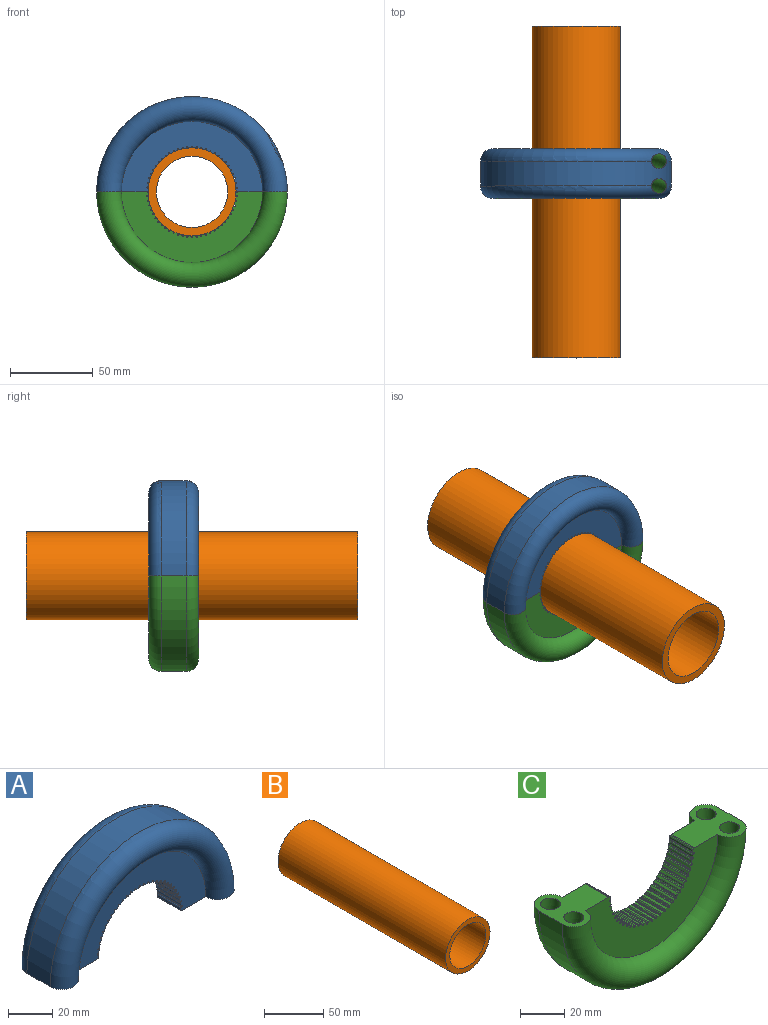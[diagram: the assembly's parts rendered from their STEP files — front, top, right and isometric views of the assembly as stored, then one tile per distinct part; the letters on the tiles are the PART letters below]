
ASSEMBLY  parts=3 mates=2
PART A: 191 faces, bbox 124.5x30x62.3 mm
  f0: cylinder r=57.5mm len=115mm, axis (0,1,0), area 2575.9mm2, adj f1,f3,f7,f8,f189,f190
  f1: torus R=50mm, axis (0,1,0), area 3629.1mm2, adj f0,f5,f7,f8,f190
  f2: torus R=50mm, axis (0,1,0), area 4103.8mm2, adj f7,f8,f190
  f3: torus R=50mm, axis (0,1,0), area 3629mm2, adj f0,f6,f7,f8,f189
  f4: torus R=50mm, axis (0,1,0), area 4103.8mm2, adj f7,f8,f189
  f5: plane 85x42.56mm, normal (0,1,0), area 1715.4mm2, adj f1,f7,f8,f9,f10,f11,f12,f13
  f6: plane 85x42.56mm, normal (0,-1,0), area 1715.4mm2, adj f3,f7,f8,f9,f10,f11,f12,f13
  f7: plane 30x30mm, normal (0,0,-1), area 499.5mm2, adj f0,f1,f2,f3,f4,f5,f6,f10
  f8: plane 30x30mm, normal (0,0,-1), area 499.5mm2, adj f0,f1,f2,f3,f4,f5,f6,f9
  f9: cylinder r=27.5mm len=15mm, axis (0,1,0), area 0.9mm2, adj f5,f6,f8,f188
  f10: plane 15x0.6mm, normal (0.21,0,-0.98), area 9.2mm2, adj f5,f6,f7,f11
  f11: cylinder r=0.5mm len=15mm, axis (0,1,0), area 9.8mm2, adj f5,f6,f10,f12
  f12: plane 15x1.18mm, normal (1,0,-0.04), area 17.7mm2, adj f5,f6,f11,f13
  f13: cylinder r=0.5mm len=15mm, axis (0,1,0), area 9.8mm2, adj f5,f6,f12,f14
  f14: plane 15x0.23mm, normal (0.3,0,0.95), area 3.6mm2, adj f5,f6,f13,f15
  f15: cylinder r=0.3mm len=15mm, axis (0,1,0), area 12.3mm2, adj f5,f6,f14,f16
  f16: plane 15x0.24mm, normal (0.11,0,-0.99), area 3.6mm2, adj f5,f6,f15,f17
  f17: cylinder r=0.5mm len=15mm, axis (0,1,0), area 9.8mm2, adj f5,f6,f16,f18
  f18: plane 15x1.17mm, normal (0.99,0,-0.15), area 17.7mm2, adj f5,f6,f17,f19
  f19: cylinder r=0.5mm len=15mm, axis (0,1,0), area 9.8mm2, adj f5,f6,f18,f20
  f20: plane 15x0.22mm, normal (0.4,0,0.92), area 3.6mm2, adj f5,f6,f19,f21
  f21: cylinder r=0.3mm len=15mm, axis (0,1,0), area 12.3mm2, adj f5,f6,f20,f22
  f22: plane 15x0.24mm, normal (0,0,-1), area 3.6mm2, adj f5,f6,f21,f23
  f23: cylinder r=0.5mm len=15mm, axis (0,1,0), area 9.8mm2, adj f5,f6,f22,f24
  f24: plane 15x1.14mm, normal (0.97,0,-0.25), area 17.7mm2, adj f5,f6,f23,f25
  f25: cylinder r=0.5mm len=15mm, axis (0,1,0), area 9.8mm2, adj f5,f6,f24,f26
  f26: plane 15x0.21mm, normal (0.49,0,0.87), area 3.6mm2, adj f5,f6,f25,f27
  f27: cylinder r=0.3mm len=15mm, axis (0,1,0), area 12.3mm2, adj f5,f6,f26,f28
  f28: plane 15x0.24mm, normal (-0.1,0,-0.99), area 3.6mm2, adj f5,f6,f27,f29
  f29: cylinder r=0.5mm len=15mm, axis (0,1,0), area 9.8mm2, adj f5,f6,f28,f30
  f30: plane 15x1.1mm, normal (0.94,0,-0.35), area 17.7mm2, adj f5,f6,f29,f31
  f31: cylinder r=0.5mm len=15mm, axis (0,1,0), area 9.8mm2, adj f5,f6,f30,f32
  f32: plane 15x0.2mm, normal (0.58,0,0.81), area 3.6mm2, adj f5,f6,f31,f33
  f33: cylinder r=0.3mm len=15mm, axis (0,1,0), area 12.3mm2, adj f5,f6,f32,f34
  f34: plane 15x0.23mm, normal (-0.21,0,-0.98), area 3.6mm2, adj f5,f6,f33,f35
  f35: cylinder r=0.5mm len=15mm, axis (0,1,0), area 9.8mm2, adj f5,f6,f34,f36
  f36: plane 15x1.05mm, normal (0.89,0,-0.45), area 17.7mm2, adj f5,f6,f35,f37
  f37: cylinder r=0.5mm len=15mm, axis (0,1,0), area 9.8mm2, adj f5,f6,f36,f38
  f38: plane 15x0.18mm, normal (0.66,0,0.75), area 3.6mm2, adj f5,f6,f37,f39
  f39: cylinder r=0.3mm len=15mm, axis (0,1,0), area 12.3mm2, adj f5,f6,f38,f40
  f40: plane 15x0.23mm, normal (-0.31,0,-0.95), area 3.6mm2, adj f5,f6,f39,f41
  f41: cylinder r=0.5mm len=15mm, axis (0,1,0), area 9.8mm2, adj f5,f6,f40,f42
  f42: plane 15x0.99mm, normal (0.84,0,-0.54), area 17.7mm2, adj f5,f6,f41,f43
  f43: cylinder r=0.5mm len=15mm, axis (0,1,0), area 9.8mm2, adj f5,f6,f42,f44
  f44: plane 15x0.18mm, normal (0.74,0,0.68), area 3.6mm2, adj f5,f6,f43,f45
  f45: cylinder r=0.3mm len=15mm, axis (0,1,0), area 12.3mm2, adj f5,f6,f44,f46
  f46: plane 15x0.22mm, normal (-0.41,0,-0.91), area 3.6mm2, adj f5,f6,f45,f47
  f47: cylinder r=0.5mm len=15mm, axis (0,1,0), area 9.8mm2, adj f5,f6,f46,f48
  f48: plane 15x0.92mm, normal (0.78,0,-0.63), area 17.7mm2, adj f5,f6,f47,f49
  f49: cylinder r=0.5mm len=15mm, axis (0,1,0), area 9.8mm2, adj f5,f6,f48,f50
  f50: plane 15x0.19mm, normal (0.8,0,0.59), area 3.6mm2, adj f5,f6,f49,f51
  f51: cylinder r=0.3mm len=15mm, axis (0,1,0), area 12.3mm2, adj f5,f6,f50,f52
  f52: plane 15x0.21mm, normal (-0.5,0,-0.87), area 3.6mm2, adj f5,f6,f51,f53
  f53: cylinder r=0.5mm len=15mm, axis (0,1,0), area 9.8mm2, adj f5,f6,f52,f54
  f54: plane 15x0.84mm, normal (0.71,0,-0.7), area 17.7mm2, adj f5,f6,f53,f55
  f55: cylinder r=0.5mm len=15mm, axis (0,1,0), area 9.8mm2, adj f5,f6,f54,f56
  f56: plane 15x0.21mm, normal (0.86,0,0.51), area 3.6mm2, adj f5,f6,f55,f57
  f57: cylinder r=0.3mm len=15mm, axis (0,1,0), area 12.3mm2, adj f5,f6,f56,f58
  f58: plane 15x0.19mm, normal (-0.59,0,-0.81), area 3.6mm2, adj f5,f6,f57,f59
  f59: cylinder r=0.5mm len=15mm, axis (0,1,0), area 9.8mm2, adj f5,f6,f58,f60
  f60: plane 15x0.92mm, normal (0.63,0,-0.78), area 17.7mm2, adj f5,f6,f59,f61
  f61: cylinder r=0.5mm len=15mm, axis (0,1,0), area 9.8mm2, adj f5,f6,f60,f62
  f62: plane 15x0.22mm, normal (0.91,0,0.41), area 3.6mm2, adj f5,f6,f61,f63
  f63: cylinder r=0.3mm len=15mm, axis (0,1,0), area 12.3mm2, adj f5,f6,f62,f64
  f64: plane 15x0.18mm, normal (-0.67,0,-0.74), area 3.6mm2, adj f5,f6,f63,f65
  f65: cylinder r=0.5mm len=15mm, axis (0,1,0), area 9.8mm2, adj f5,f6,f64,f66
  f66: plane 15x0.99mm, normal (0.55,0,-0.84), area 17.7mm2, adj f5,f6,f65,f67
  f67: cylinder r=0.5mm len=15mm, axis (0,1,0), area 9.8mm2, adj f5,f6,f66,f68
  f68: plane 15x0.23mm, normal (0.95,0,0.31), area 3.6mm2, adj f5,f6,f67,f69
  f69: cylinder r=0.3mm len=15mm, axis (0,1,0), area 12.3mm2, adj f5,f6,f68,f70
  f70: plane 15x0.18mm, normal (-0.74,0,-0.67), area 3.6mm2, adj f5,f6,f69,f71
  f71: cylinder r=0.5mm len=15mm, axis (0,1,0), area 9.8mm2, adj f5,f6,f70,f72
  f72: plane 15x1.05mm, normal (0.46,0,-0.89), area 17.7mm2, adj f5,f6,f71,f73
  f73: cylinder r=0.5mm len=15mm, axis (0,1,0), area 9.8mm2, adj f5,f6,f72,f74
  f74: plane 15x0.23mm, normal (0.98,0,0.21), area 3.6mm2, adj f5,f6,f73,f75
  f75: cylinder r=0.3mm len=15mm, axis (0,1,0), area 12.3mm2, adj f5,f6,f74,f76
  f76: plane 15x0.19mm, normal (-0.81,0,-0.59), area 3.6mm2, adj f5,f6,f75,f77
  f77: cylinder r=0.5mm len=15mm, axis (0,1,0), area 9.8mm2, adj f5,f6,f76,f78
  f78: plane 15x1.1mm, normal (0.36,0,-0.93), area 17.7mm2, adj f5,f6,f77,f79
  f79: cylinder r=0.5mm len=15mm, axis (0,1,0), area 9.8mm2, adj f5,f6,f78,f80
  f80: plane 15x0.24mm, normal (0.99,0,0.11), area 3.6mm2, adj f5,f6,f79,f81
  f81: cylinder r=0.3mm len=15mm, axis (0,1,0), area 12.3mm2, adj f5,f6,f80,f82
  f82: plane 15x0.21mm, normal (-0.87,0,-0.5), area 3.6mm2, adj f5,f6,f81,f83
  f83: cylinder r=0.5mm len=15mm, axis (0,1,0), area 9.8mm2, adj f5,f6,f82,f84
  f84: plane 15x1.14mm, normal (0.26,0,-0.97), area 17.7mm2, adj f5,f6,f83,f85
  f85: cylinder r=0.5mm len=15mm, axis (0,1,0), area 9.8mm2, adj f5,f6,f84,f86
  f86: plane 15x0.24mm, normal (1,0,0), area 3.6mm2, adj f5,f6,f85,f87
  f87: cylinder r=0.3mm len=15mm, axis (0,1,0), area 12.3mm2, adj f5,f6,f86,f88
  f88: plane 15x0.22mm, normal (-0.92,0,-0.4), area 3.6mm2, adj f5,f6,f87,f89
  f89: cylinder r=0.5mm len=15mm, axis (0,1,0), area 9.8mm2, adj f5,f6,f88,f90
  f90: plane 15x1.17mm, normal (0.16,0,-0.99), area 17.7mm2, adj f5,f6,f89,f91
  f91: cylinder r=0.5mm len=15mm, axis (0,1,0), area 9.8mm2, adj f5,f6,f90,f92
  f92: plane 15x0.24mm, normal (0.99,0,-0.1), area 3.6mm2, adj f5,f6,f91,f93
  f93: cylinder r=0.3mm len=15mm, axis (0,1,0), area 12.3mm2, adj f5,f6,f92,f94
  f94: plane 15x0.23mm, normal (-0.95,0,-0.3), area 3.6mm2, adj f5,f6,f93,f95
  f95: cylinder r=0.5mm len=15mm, axis (0,1,0), area 9.8mm2, adj f5,f6,f94,f96
  f96: plane 15x1.18mm, normal (0.05,0,-1), area 17.7mm2, adj f5,f6,f95,f97
  f97: cylinder r=0.5mm len=15mm, axis (0,1,0), area 9.8mm2, adj f5,f6,f96,f98
  f98: plane 15x0.23mm, normal (0.98,0,-0.21), area 3.6mm2, adj f5,f6,f97,f99
  f99: cylinder r=0.3mm len=15mm, axis (0,1,0), area 12.3mm2, adj f5,f6,f98,f100
  f100: plane 15x0.23mm, normal (-0.98,0,-0.2), area 3.6mm2, adj f5,f6,f99,f101
  f101: cylinder r=0.5mm len=15mm, axis (0,1,0), area 9.8mm2, adj f5,f6,f100,f102
  f102: plane 15x1.18mm, normal (-0.05,0,-1), area 17.7mm2, adj f5,f6,f101,f103
  f103: cylinder r=0.5mm len=15mm, axis (0,1,0), area 9.8mm2, adj f5,f6,f102,f104
  f104: plane 15x0.23mm, normal (0.95,0,-0.31), area 3.6mm2, adj f5,f6,f103,f105
  f105: cylinder r=0.3mm len=15mm, axis (0,1,0), area 12.3mm2, adj f5,f6,f104,f106
  f106: plane 15x0.24mm, normal (-1,0,-0.1), area 3.6mm2, adj f5,f6,f105,f107
  f107: cylinder r=0.5mm len=15mm, axis (0,1,0), area 9.8mm2, adj f5,f6,f106,f108
  f108: plane 15x1.17mm, normal (-0.16,0,-0.99), area 17.7mm2, adj f5,f6,f107,f109
  f109: cylinder r=0.5mm len=15mm, axis (0,1,0), area 9.8mm2, adj f5,f6,f108,f110
  f110: plane 15x0.22mm, normal (0.91,0,-0.41), area 3.6mm2, adj f5,f6,f109,f111
  f111: cylinder r=0.3mm len=15mm, axis (0,1,0), area 12.3mm2, adj f5,f6,f110,f112
  f112: plane 15x0.24mm, normal (-1,0,0.01), area 3.6mm2, adj f5,f6,f111,f113
  f113: cylinder r=0.5mm len=15mm, axis (0,1,0), area 9.8mm2, adj f5,f6,f112,f114
  f114: plane 15x1.14mm, normal (-0.26,0,-0.97), area 17.7mm2, adj f5,f6,f113,f115
  f115: cylinder r=0.5mm len=15mm, axis (0,1,0), area 9.8mm2, adj f5,f6,f114,f116
  f116: plane 15x0.21mm, normal (0.87,0,-0.5), area 3.6mm2, adj f5,f6,f115,f117
  f117: cylinder r=0.3mm len=15mm, axis (0,1,0), area 12.3mm2, adj f5,f6,f116,f118
  f118: plane 15x0.24mm, normal (-0.99,0,0.11), area 3.6mm2, adj f5,f6,f117,f119
  f119: cylinder r=0.5mm len=15mm, axis (0,1,0), area 9.8mm2, adj f5,f6,f118,f120
  f120: plane 15x1.1mm, normal (-0.36,0,-0.93), area 17.7mm2, adj f5,f6,f119,f121
  f121: cylinder r=0.5mm len=15mm, axis (0,1,0), area 9.8mm2, adj f5,f6,f120,f122
  f122: plane 15x0.19mm, normal (0.81,0,-0.59), area 3.6mm2, adj f5,f6,f121,f123
  f123: cylinder r=0.3mm len=15mm, axis (0,1,0), area 12.3mm2, adj f5,f6,f122,f124
  f124: plane 15x0.23mm, normal (-0.98,0,0.21), area 3.6mm2, adj f5,f6,f123,f125
  f125: cylinder r=0.5mm len=15mm, axis (0,1,0), area 9.8mm2, adj f5,f6,f124,f126
  f126: plane 15x1.05mm, normal (-0.46,0,-0.89), area 17.7mm2, adj f5,f6,f125,f127
  f127: cylinder r=0.5mm len=15mm, axis (0,1,0), area 9.8mm2, adj f5,f6,f126,f128
  f128: plane 15x0.18mm, normal (0.74,0,-0.67), area 3.6mm2, adj f5,f6,f127,f129
  f129: cylinder r=0.3mm len=15mm, axis (0,1,0), area 12.3mm2, adj f5,f6,f128,f130
  f130: plane 15x0.23mm, normal (-0.95,0,0.32), area 3.6mm2, adj f5,f6,f129,f131
  f131: cylinder r=0.5mm len=15mm, axis (0,1,0), area 9.8mm2, adj f5,f6,f130,f132
  f132: plane 15x0.99mm, normal (-0.55,0,-0.84), area 17.7mm2, adj f5,f6,f131,f133
  f133: cylinder r=0.5mm len=15mm, axis (0,1,0), area 9.8mm2, adj f5,f6,f132,f134
  f134: plane 15x0.18mm, normal (0.67,0,-0.74), area 3.6mm2, adj f5,f6,f133,f135
  f135: cylinder r=0.3mm len=15mm, axis (0,1,0), area 12.3mm2, adj f5,f6,f134,f136
  f136: plane 15x0.22mm, normal (-0.91,0,0.41), area 3.6mm2, adj f5,f6,f135,f137
  f137: cylinder r=0.5mm len=15mm, axis (0,1,0), area 9.8mm2, adj f5,f6,f136,f138
  f138: plane 15x0.91mm, normal (-0.63,0,-0.77), area 17.7mm2, adj f5,f6,f137,f139
  f139: cylinder r=0.5mm len=15mm, axis (0,1,0), area 9.8mm2, adj f5,f6,f138,f140
  f140: plane 15x0.19mm, normal (0.59,0,-0.81), area 3.6mm2, adj f5,f6,f139,f141
  f141: cylinder r=0.3mm len=15mm, axis (0,1,0), area 12.3mm2, adj f5,f6,f140,f142
  f142: plane 15x0.21mm, normal (-0.86,0,0.51), area 3.6mm2, adj f5,f6,f141,f143
  f143: cylinder r=0.5mm len=15mm, axis (0,1,0), area 9.8mm2, adj f5,f6,f142,f144
  f144: plane 15x0.84mm, normal (-0.71,0,-0.7), area 17.7mm2, adj f5,f6,f143,f145
  f145: cylinder r=0.5mm len=15mm, axis (0,1,0), area 9.8mm2, adj f5,f6,f144,f146
  f146: plane 15x0.21mm, normal (0.5,0,-0.87), area 3.6mm2, adj f5,f6,f145,f147
  f147: cylinder r=0.3mm len=15mm, axis (0,1,0), area 12.3mm2, adj f5,f6,f146,f148
  f148: plane 15x0.19mm, normal (-0.8,0,0.6), area 3.6mm2, adj f5,f6,f147,f149
  f149: cylinder r=0.5mm len=15mm, axis (0,1,0), area 9.8mm2, adj f5,f6,f148,f150
  f150: plane 15x0.92mm, normal (-0.78,0,-0.62), area 17.7mm2, adj f5,f6,f149,f151
  f151: cylinder r=0.5mm len=15mm, axis (0,1,0), area 9.8mm2, adj f5,f6,f150,f152
  f152: plane 15x0.22mm, normal (0.4,0,-0.91), area 3.6mm2, adj f5,f6,f151,f153
  f153: cylinder r=0.3mm len=15mm, axis (0,1,0), area 12.3mm2, adj f5,f6,f152,f154
  f154: plane 15x0.18mm, normal (-0.74,0,0.68), area 3.6mm2, adj f5,f6,f153,f155
  f155: cylinder r=0.5mm len=15mm, axis (0,1,0), area 9.8mm2, adj f5,f6,f154,f156
  f156: plane 15x0.99mm, normal (-0.84,0,-0.54), area 17.7mm2, adj f5,f6,f155,f157
  f157: cylinder r=0.5mm len=15mm, axis (0,1,0), area 9.8mm2, adj f5,f6,f156,f158
  f158: plane 15x0.23mm, normal (0.31,0,-0.95), area 3.6mm2, adj f5,f6,f157,f159
  f159: cylinder r=0.3mm len=15mm, axis (0,1,0), area 12.3mm2, adj f5,f6,f158,f160
  f160: plane 15x0.18mm, normal (-0.66,0,0.75), area 3.6mm2, adj f5,f6,f159,f161
  f161: cylinder r=0.5mm len=15mm, axis (0,1,0), area 9.8mm2, adj f5,f6,f160,f162
  f162: plane 15x1.06mm, normal (-0.89,0,-0.45), area 17.7mm2, adj f5,f6,f161,f163
  f163: cylinder r=0.5mm len=15mm, axis (0,1,0), area 9.8mm2, adj f5,f6,f162,f164
  f164: plane 15x0.23mm, normal (0.2,0,-0.98), area 3.6mm2, adj f5,f6,f163,f165
  f165: cylinder r=0.3mm len=15mm, axis (0,1,0), area 12.3mm2, adj f5,f6,f164,f166
  f166: plane 15x0.2mm, normal (-0.58,0,0.82), area 3.6mm2, adj f5,f6,f165,f167
  f167: cylinder r=0.5mm len=15mm, axis (0,1,0), area 9.8mm2, adj f5,f6,f166,f168
  f168: plane 15x1.11mm, normal (-0.94,0,-0.35), area 17.7mm2, adj f5,f6,f167,f169
  f169: cylinder r=0.5mm len=15mm, axis (0,1,0), area 9.8mm2, adj f5,f6,f168,f170
  f170: plane 15x0.24mm, normal (0.1,0,-0.99), area 3.6mm2, adj f5,f6,f169,f171
  f171: cylinder r=0.3mm len=15mm, axis (0,1,0), area 12.3mm2, adj f5,f6,f170,f172
  f172: plane 15x0.21mm, normal (-0.49,0,0.87), area 3.6mm2, adj f5,f6,f171,f173
  f173: cylinder r=0.5mm len=15mm, axis (0,1,0), area 9.8mm2, adj f5,f6,f172,f174
  f174: plane 15x1.14mm, normal (-0.97,0,-0.25), area 17.7mm2, adj f5,f6,f173,f175
  f175: cylinder r=0.5mm len=15mm, axis (0,1,0), area 9.8mm2, adj f5,f6,f174,f176
  f176: plane 15x0.24mm, normal (-0.01,0,-1), area 3.6mm2, adj f5,f6,f175,f177
  f177: cylinder r=0.3mm len=15mm, axis (0,1,0), area 12.3mm2, adj f5,f6,f176,f178
  f178: plane 15x0.22mm, normal (-0.4,0,0.92), area 3.6mm2, adj f5,f6,f177,f179
  f179: cylinder r=0.5mm len=15mm, axis (0,1,0), area 9.8mm2, adj f5,f6,f178,f180
  f180: plane 15x1.17mm, normal (-0.99,0,-0.15), area 17.7mm2, adj f5,f6,f179,f181
  f181: cylinder r=0.5mm len=15mm, axis (0,1,0), area 9.8mm2, adj f5,f6,f180,f182
  f182: plane 15x0.24mm, normal (-0.11,0,-0.99), area 3.6mm2, adj f5,f6,f181,f183
  f183: cylinder r=0.3mm len=15mm, axis (0,1,0), area 12.3mm2, adj f5,f6,f182,f184
  f184: plane 15x0.23mm, normal (-0.3,0,0.96), area 3.6mm2, adj f5,f6,f183,f185
  f185: cylinder r=0.5mm len=15mm, axis (0,1,0), area 9.8mm2, adj f5,f6,f184,f186
  f186: plane 15x1.18mm, normal (-1,0,-0.04), area 17.7mm2, adj f5,f6,f185,f187
  f187: cylinder r=0.5mm len=15mm, axis (0,1,0), area 9.8mm2, adj f5,f6,f186,f188
  f188: plane 15x0.6mm, normal (-0.21,0,-0.98), area 9.2mm2, adj f5,f6,f9,f187
  f189: cylinder r=4.5mm len=35.16mm, axis (0,0,-1), area 434.3mm2, adj f0,f3,f4,f8
  f190: cylinder r=4.5mm len=35.16mm, axis (0,0,-1), area 434.3mm2, adj f0,f1,f2,f8
PART B: 4 faces, bbox 53x200x53 mm
  f0: cylinder r=21.5mm len=200mm, axis (0,1,0), area 27017.7mm2, adj f2,f3
  f1: cylinder r=26.5mm len=200mm, axis (0,1,0), area 33300.9mm2, adj f2,f3
  f2: plane 53x53mm, normal (0,-1,0), area 754mm2, adj f0,f1
  f3: plane 53x53mm, normal (0,1,0), area 754mm2, adj f0,f1
PART C: 189 faces, bbox 124.5x30x62.3 mm
  f0: cylinder r=57.5mm len=115mm, axis (0,1,0), area 2709.6mm2, adj f1,f5,f7,f8
  f1: torus R=50mm, axis (0,1,0), area 3701.1mm2, adj f0,f2,f7,f8
  f2: plane 85x42.56mm, normal (0,1,0), area 1715.4mm2, adj f1,f7,f8,f9,f10,f11,f12,f13
  f3: plane 85x42.56mm, normal (0,-1,0), area 1715.4mm2, adj f5,f7,f8,f9,f10,f11,f12,f13
  f4: torus R=50mm, axis (0,1,0), area 4441.3mm2, adj f7,f8
  f5: torus R=50mm, axis (0,1,0), area 3701.1mm2, adj f0,f3,f7,f8
  f6: torus R=50mm, axis (0,1,0), area 4441.3mm2, adj f7,f8
  f7: plane 30x30mm, normal (0,0,1), area 499.5mm2, adj f0,f1,f2,f3,f4,f5,f6,f10
  f8: plane 30x30mm, normal (0,0,1), area 499.5mm2, adj f0,f1,f2,f3,f4,f5,f6,f9
  f9: cylinder r=27.5mm len=15mm, axis (0,1,0), area 0.9mm2, adj f2,f3,f8,f188
  f10: plane 15x0.6mm, normal (-0.21,0,0.98), area 9.2mm2, adj f2,f3,f7,f11
  f11: cylinder r=0.5mm len=15mm, axis (0,1,0), area 9.8mm2, adj f2,f3,f10,f12
  f12: plane 15x1.18mm, normal (-1,0,0.04), area 17.7mm2, adj f2,f3,f11,f13
  f13: cylinder r=0.5mm len=15mm, axis (0,1,0), area 9.8mm2, adj f2,f3,f12,f14
  f14: plane 15x0.23mm, normal (-0.3,0,-0.95), area 3.6mm2, adj f2,f3,f13,f15
  f15: cylinder r=0.3mm len=15mm, axis (0,1,0), area 12.3mm2, adj f2,f3,f14,f16
  f16: plane 15x0.24mm, normal (-0.11,0,0.99), area 3.6mm2, adj f2,f3,f15,f17
  f17: cylinder r=0.5mm len=15mm, axis (0,1,0), area 9.8mm2, adj f2,f3,f16,f18
  f18: plane 15x1.17mm, normal (-0.99,0,0.15), area 17.7mm2, adj f2,f3,f17,f19
  f19: cylinder r=0.5mm len=15mm, axis (0,1,0), area 9.8mm2, adj f2,f3,f18,f20
  f20: plane 15x0.22mm, normal (-0.4,0,-0.92), area 3.6mm2, adj f2,f3,f19,f21
  f21: cylinder r=0.3mm len=15mm, axis (0,1,0), area 12.3mm2, adj f2,f3,f20,f22
  f22: plane 15x0.24mm, normal (0,0,1), area 3.6mm2, adj f2,f3,f21,f23
  f23: cylinder r=0.5mm len=15mm, axis (0,1,0), area 9.8mm2, adj f2,f3,f22,f24
  f24: plane 15x1.14mm, normal (-0.97,0,0.25), area 17.7mm2, adj f2,f3,f23,f25
  f25: cylinder r=0.5mm len=15mm, axis (0,1,0), area 9.8mm2, adj f2,f3,f24,f26
  f26: plane 15x0.21mm, normal (-0.49,0,-0.87), area 3.6mm2, adj f2,f3,f25,f27
  f27: cylinder r=0.3mm len=15mm, axis (0,1,0), area 12.3mm2, adj f2,f3,f26,f28
  f28: plane 15x0.24mm, normal (0.1,0,0.99), area 3.6mm2, adj f2,f3,f27,f29
  f29: cylinder r=0.5mm len=15mm, axis (0,1,0), area 9.8mm2, adj f2,f3,f28,f30
  f30: plane 15x1.1mm, normal (-0.94,0,0.35), area 17.7mm2, adj f2,f3,f29,f31
  f31: cylinder r=0.5mm len=15mm, axis (0,1,0), area 9.8mm2, adj f2,f3,f30,f32
  f32: plane 15x0.2mm, normal (-0.58,0,-0.81), area 3.6mm2, adj f2,f3,f31,f33
  f33: cylinder r=0.3mm len=15mm, axis (0,1,0), area 12.3mm2, adj f2,f3,f32,f34
  f34: plane 15x0.23mm, normal (0.21,0,0.98), area 3.6mm2, adj f2,f3,f33,f35
  f35: cylinder r=0.5mm len=15mm, axis (0,1,0), area 9.8mm2, adj f2,f3,f34,f36
  f36: plane 15x1.05mm, normal (-0.89,0,0.45), area 17.7mm2, adj f2,f3,f35,f37
  f37: cylinder r=0.5mm len=15mm, axis (0,1,0), area 9.8mm2, adj f2,f3,f36,f38
  f38: plane 15x0.18mm, normal (-0.66,0,-0.75), area 3.6mm2, adj f2,f3,f37,f39
  f39: cylinder r=0.3mm len=15mm, axis (0,1,0), area 12.3mm2, adj f2,f3,f38,f40
  f40: plane 15x0.23mm, normal (0.31,0,0.95), area 3.6mm2, adj f2,f3,f39,f41
  f41: cylinder r=0.5mm len=15mm, axis (0,1,0), area 9.8mm2, adj f2,f3,f40,f42
  f42: plane 15x0.99mm, normal (-0.84,0,0.54), area 17.7mm2, adj f2,f3,f41,f43
  f43: cylinder r=0.5mm len=15mm, axis (0,1,0), area 9.8mm2, adj f2,f3,f42,f44
  f44: plane 15x0.18mm, normal (-0.74,0,-0.68), area 3.6mm2, adj f2,f3,f43,f45
  f45: cylinder r=0.3mm len=15mm, axis (0,1,0), area 12.3mm2, adj f2,f3,f44,f46
  f46: plane 15x0.22mm, normal (0.41,0,0.91), area 3.6mm2, adj f2,f3,f45,f47
  f47: cylinder r=0.5mm len=15mm, axis (0,1,0), area 9.8mm2, adj f2,f3,f46,f48
  f48: plane 15x0.92mm, normal (-0.78,0,0.63), area 17.7mm2, adj f2,f3,f47,f49
  f49: cylinder r=0.5mm len=15mm, axis (0,1,0), area 9.8mm2, adj f2,f3,f48,f50
  f50: plane 15x0.19mm, normal (-0.8,0,-0.59), area 3.6mm2, adj f2,f3,f49,f51
  f51: cylinder r=0.3mm len=15mm, axis (0,1,0), area 12.3mm2, adj f2,f3,f50,f52
  f52: plane 15x0.21mm, normal (0.5,0,0.87), area 3.6mm2, adj f2,f3,f51,f53
  f53: cylinder r=0.5mm len=15mm, axis (0,1,0), area 9.8mm2, adj f2,f3,f52,f54
  f54: plane 15x0.84mm, normal (-0.71,0,0.7), area 17.7mm2, adj f2,f3,f53,f55
  f55: cylinder r=0.5mm len=15mm, axis (0,1,0), area 9.8mm2, adj f2,f3,f54,f56
  f56: plane 15x0.21mm, normal (-0.86,0,-0.51), area 3.6mm2, adj f2,f3,f55,f57
  f57: cylinder r=0.3mm len=15mm, axis (0,1,0), area 12.3mm2, adj f2,f3,f56,f58
  f58: plane 15x0.19mm, normal (0.59,0,0.81), area 3.6mm2, adj f2,f3,f57,f59
  f59: cylinder r=0.5mm len=15mm, axis (0,1,0), area 9.8mm2, adj f2,f3,f58,f60
  f60: plane 15x0.92mm, normal (-0.63,0,0.78), area 17.7mm2, adj f2,f3,f59,f61
  f61: cylinder r=0.5mm len=15mm, axis (0,1,0), area 9.8mm2, adj f2,f3,f60,f62
  f62: plane 15x0.22mm, normal (-0.91,0,-0.41), area 3.6mm2, adj f2,f3,f61,f63
  f63: cylinder r=0.3mm len=15mm, axis (0,1,0), area 12.3mm2, adj f2,f3,f62,f64
  f64: plane 15x0.18mm, normal (0.67,0,0.74), area 3.6mm2, adj f2,f3,f63,f65
  f65: cylinder r=0.5mm len=15mm, axis (0,1,0), area 9.8mm2, adj f2,f3,f64,f66
  f66: plane 15x0.99mm, normal (-0.55,0,0.84), area 17.7mm2, adj f2,f3,f65,f67
  f67: cylinder r=0.5mm len=15mm, axis (0,1,0), area 9.8mm2, adj f2,f3,f66,f68
  f68: plane 15x0.23mm, normal (-0.95,0,-0.31), area 3.6mm2, adj f2,f3,f67,f69
  f69: cylinder r=0.3mm len=15mm, axis (0,1,0), area 12.3mm2, adj f2,f3,f68,f70
  f70: plane 15x0.18mm, normal (0.74,0,0.67), area 3.6mm2, adj f2,f3,f69,f71
  f71: cylinder r=0.5mm len=15mm, axis (0,1,0), area 9.8mm2, adj f2,f3,f70,f72
  f72: plane 15x1.05mm, normal (-0.46,0,0.89), area 17.7mm2, adj f2,f3,f71,f73
  f73: cylinder r=0.5mm len=15mm, axis (0,1,0), area 9.8mm2, adj f2,f3,f72,f74
  f74: plane 15x0.23mm, normal (-0.98,0,-0.21), area 3.6mm2, adj f2,f3,f73,f75
  f75: cylinder r=0.3mm len=15mm, axis (0,1,0), area 12.3mm2, adj f2,f3,f74,f76
  f76: plane 15x0.19mm, normal (0.81,0,0.59), area 3.6mm2, adj f2,f3,f75,f77
  f77: cylinder r=0.5mm len=15mm, axis (0,1,0), area 9.8mm2, adj f2,f3,f76,f78
  f78: plane 15x1.1mm, normal (-0.36,0,0.93), area 17.7mm2, adj f2,f3,f77,f79
  f79: cylinder r=0.5mm len=15mm, axis (0,1,0), area 9.8mm2, adj f2,f3,f78,f80
  f80: plane 15x0.24mm, normal (-0.99,0,-0.11), area 3.6mm2, adj f2,f3,f79,f81
  f81: cylinder r=0.3mm len=15mm, axis (0,1,0), area 12.3mm2, adj f2,f3,f80,f82
  f82: plane 15x0.21mm, normal (0.87,0,0.5), area 3.6mm2, adj f2,f3,f81,f83
  f83: cylinder r=0.5mm len=15mm, axis (0,1,0), area 9.8mm2, adj f2,f3,f82,f84
  f84: plane 15x1.14mm, normal (-0.26,0,0.97), area 17.7mm2, adj f2,f3,f83,f85
  f85: cylinder r=0.5mm len=15mm, axis (0,1,0), area 9.8mm2, adj f2,f3,f84,f86
  f86: plane 15x0.24mm, normal (-1,0,0), area 3.6mm2, adj f2,f3,f85,f87
  f87: cylinder r=0.3mm len=15mm, axis (0,1,0), area 12.3mm2, adj f2,f3,f86,f88
  f88: plane 15x0.22mm, normal (0.92,0,0.4), area 3.6mm2, adj f2,f3,f87,f89
  f89: cylinder r=0.5mm len=15mm, axis (0,1,0), area 9.8mm2, adj f2,f3,f88,f90
  f90: plane 15x1.17mm, normal (-0.16,0,0.99), area 17.7mm2, adj f2,f3,f89,f91
  f91: cylinder r=0.5mm len=15mm, axis (0,1,0), area 9.8mm2, adj f2,f3,f90,f92
  f92: plane 15x0.24mm, normal (-0.99,0,0.1), area 3.6mm2, adj f2,f3,f91,f93
  f93: cylinder r=0.3mm len=15mm, axis (0,1,0), area 12.3mm2, adj f2,f3,f92,f94
  f94: plane 15x0.23mm, normal (0.95,0,0.3), area 3.6mm2, adj f2,f3,f93,f95
  f95: cylinder r=0.5mm len=15mm, axis (0,1,0), area 9.8mm2, adj f2,f3,f94,f96
  f96: plane 15x1.18mm, normal (-0.05,0,1), area 17.7mm2, adj f2,f3,f95,f97
  f97: cylinder r=0.5mm len=15mm, axis (0,1,0), area 9.8mm2, adj f2,f3,f96,f98
  f98: plane 15x0.23mm, normal (-0.98,0,0.21), area 3.6mm2, adj f2,f3,f97,f99
  f99: cylinder r=0.3mm len=15mm, axis (0,1,0), area 12.3mm2, adj f2,f3,f98,f100
  f100: plane 15x0.23mm, normal (0.98,0,0.2), area 3.6mm2, adj f2,f3,f99,f101
  f101: cylinder r=0.5mm len=15mm, axis (0,1,0), area 9.8mm2, adj f2,f3,f100,f102
  f102: plane 15x1.18mm, normal (0.05,0,1), area 17.7mm2, adj f2,f3,f101,f103
  f103: cylinder r=0.5mm len=15mm, axis (0,1,0), area 9.8mm2, adj f2,f3,f102,f104
  f104: plane 15x0.23mm, normal (-0.95,0,0.31), area 3.6mm2, adj f2,f3,f103,f105
  f105: cylinder r=0.3mm len=15mm, axis (0,1,0), area 12.3mm2, adj f2,f3,f104,f106
  f106: plane 15x0.24mm, normal (1,0,0.1), area 3.6mm2, adj f2,f3,f105,f107
  f107: cylinder r=0.5mm len=15mm, axis (0,1,0), area 9.8mm2, adj f2,f3,f106,f108
  f108: plane 15x1.17mm, normal (0.16,0,0.99), area 17.7mm2, adj f2,f3,f107,f109
  f109: cylinder r=0.5mm len=15mm, axis (0,1,0), area 9.8mm2, adj f2,f3,f108,f110
  f110: plane 15x0.22mm, normal (-0.91,0,0.41), area 3.6mm2, adj f2,f3,f109,f111
  f111: cylinder r=0.3mm len=15mm, axis (0,1,0), area 12.3mm2, adj f2,f3,f110,f112
  f112: plane 15x0.24mm, normal (1,0,-0.01), area 3.6mm2, adj f2,f3,f111,f113
  f113: cylinder r=0.5mm len=15mm, axis (0,1,0), area 9.8mm2, adj f2,f3,f112,f114
  f114: plane 15x1.14mm, normal (0.26,0,0.97), area 17.7mm2, adj f2,f3,f113,f115
  f115: cylinder r=0.5mm len=15mm, axis (0,1,0), area 9.8mm2, adj f2,f3,f114,f116
  f116: plane 15x0.21mm, normal (-0.87,0,0.5), area 3.6mm2, adj f2,f3,f115,f117
  f117: cylinder r=0.3mm len=15mm, axis (0,1,0), area 12.3mm2, adj f2,f3,f116,f118
  f118: plane 15x0.24mm, normal (0.99,0,-0.11), area 3.6mm2, adj f2,f3,f117,f119
  f119: cylinder r=0.5mm len=15mm, axis (0,1,0), area 9.8mm2, adj f2,f3,f118,f120
  f120: plane 15x1.1mm, normal (0.36,0,0.93), area 17.7mm2, adj f2,f3,f119,f121
  f121: cylinder r=0.5mm len=15mm, axis (0,1,0), area 9.8mm2, adj f2,f3,f120,f122
  f122: plane 15x0.19mm, normal (-0.81,0,0.59), area 3.6mm2, adj f2,f3,f121,f123
  f123: cylinder r=0.3mm len=15mm, axis (0,1,0), area 12.3mm2, adj f2,f3,f122,f124
  f124: plane 15x0.23mm, normal (0.98,0,-0.21), area 3.6mm2, adj f2,f3,f123,f125
  f125: cylinder r=0.5mm len=15mm, axis (0,1,0), area 9.8mm2, adj f2,f3,f124,f126
  f126: plane 15x1.05mm, normal (0.46,0,0.89), area 17.7mm2, adj f2,f3,f125,f127
  f127: cylinder r=0.5mm len=15mm, axis (0,1,0), area 9.8mm2, adj f2,f3,f126,f128
  f128: plane 15x0.18mm, normal (-0.74,0,0.67), area 3.6mm2, adj f2,f3,f127,f129
  f129: cylinder r=0.3mm len=15mm, axis (0,1,0), area 12.3mm2, adj f2,f3,f128,f130
  f130: plane 15x0.23mm, normal (0.95,0,-0.32), area 3.6mm2, adj f2,f3,f129,f131
  f131: cylinder r=0.5mm len=15mm, axis (0,1,0), area 9.8mm2, adj f2,f3,f130,f132
  f132: plane 15x0.99mm, normal (0.55,0,0.84), area 17.7mm2, adj f2,f3,f131,f133
  f133: cylinder r=0.5mm len=15mm, axis (0,1,0), area 9.8mm2, adj f2,f3,f132,f134
  f134: plane 15x0.18mm, normal (-0.67,0,0.74), area 3.6mm2, adj f2,f3,f133,f135
  f135: cylinder r=0.3mm len=15mm, axis (0,1,0), area 12.3mm2, adj f2,f3,f134,f136
  f136: plane 15x0.22mm, normal (0.91,0,-0.41), area 3.6mm2, adj f2,f3,f135,f137
  f137: cylinder r=0.5mm len=15mm, axis (0,1,0), area 9.8mm2, adj f2,f3,f136,f138
  f138: plane 15x0.91mm, normal (0.63,0,0.77), area 17.7mm2, adj f2,f3,f137,f139
  f139: cylinder r=0.5mm len=15mm, axis (0,1,0), area 9.8mm2, adj f2,f3,f138,f140
  f140: plane 15x0.19mm, normal (-0.59,0,0.81), area 3.6mm2, adj f2,f3,f139,f141
  f141: cylinder r=0.3mm len=15mm, axis (0,1,0), area 12.3mm2, adj f2,f3,f140,f142
  f142: plane 15x0.21mm, normal (0.86,0,-0.51), area 3.6mm2, adj f2,f3,f141,f143
  f143: cylinder r=0.5mm len=15mm, axis (0,1,0), area 9.8mm2, adj f2,f3,f142,f144
  f144: plane 15x0.84mm, normal (0.71,0,0.7), area 17.7mm2, adj f2,f3,f143,f145
  f145: cylinder r=0.5mm len=15mm, axis (0,1,0), area 9.8mm2, adj f2,f3,f144,f146
  f146: plane 15x0.21mm, normal (-0.5,0,0.87), area 3.6mm2, adj f2,f3,f145,f147
  f147: cylinder r=0.3mm len=15mm, axis (0,1,0), area 12.3mm2, adj f2,f3,f146,f148
  f148: plane 15x0.19mm, normal (0.8,0,-0.6), area 3.6mm2, adj f2,f3,f147,f149
  f149: cylinder r=0.5mm len=15mm, axis (0,1,0), area 9.8mm2, adj f2,f3,f148,f150
  f150: plane 15x0.92mm, normal (0.78,0,0.62), area 17.7mm2, adj f2,f3,f149,f151
  f151: cylinder r=0.5mm len=15mm, axis (0,1,0), area 9.8mm2, adj f2,f3,f150,f152
  f152: plane 15x0.22mm, normal (-0.4,0,0.91), area 3.6mm2, adj f2,f3,f151,f153
  f153: cylinder r=0.3mm len=15mm, axis (0,1,0), area 12.3mm2, adj f2,f3,f152,f154
  f154: plane 15x0.18mm, normal (0.74,0,-0.68), area 3.6mm2, adj f2,f3,f153,f155
  f155: cylinder r=0.5mm len=15mm, axis (0,1,0), area 9.8mm2, adj f2,f3,f154,f156
  f156: plane 15x0.99mm, normal (0.84,0,0.54), area 17.7mm2, adj f2,f3,f155,f157
  f157: cylinder r=0.5mm len=15mm, axis (0,1,0), area 9.8mm2, adj f2,f3,f156,f158
  f158: plane 15x0.23mm, normal (-0.31,0,0.95), area 3.6mm2, adj f2,f3,f157,f159
  f159: cylinder r=0.3mm len=15mm, axis (0,1,0), area 12.3mm2, adj f2,f3,f158,f160
  f160: plane 15x0.18mm, normal (0.66,0,-0.75), area 3.6mm2, adj f2,f3,f159,f161
  f161: cylinder r=0.5mm len=15mm, axis (0,1,0), area 9.8mm2, adj f2,f3,f160,f162
  f162: plane 15x1.06mm, normal (0.89,0,0.45), area 17.7mm2, adj f2,f3,f161,f163
  f163: cylinder r=0.5mm len=15mm, axis (0,1,0), area 9.8mm2, adj f2,f3,f162,f164
  f164: plane 15x0.23mm, normal (-0.2,0,0.98), area 3.6mm2, adj f2,f3,f163,f165
  f165: cylinder r=0.3mm len=15mm, axis (0,1,0), area 12.3mm2, adj f2,f3,f164,f166
  f166: plane 15x0.2mm, normal (0.58,0,-0.82), area 3.6mm2, adj f2,f3,f165,f167
  f167: cylinder r=0.5mm len=15mm, axis (0,1,0), area 9.8mm2, adj f2,f3,f166,f168
  f168: plane 15x1.11mm, normal (0.94,0,0.35), area 17.7mm2, adj f2,f3,f167,f169
  f169: cylinder r=0.5mm len=15mm, axis (0,1,0), area 9.8mm2, adj f2,f3,f168,f170
  f170: plane 15x0.24mm, normal (-0.1,0,0.99), area 3.6mm2, adj f2,f3,f169,f171
  f171: cylinder r=0.3mm len=15mm, axis (0,1,0), area 12.3mm2, adj f2,f3,f170,f172
  f172: plane 15x0.21mm, normal (0.49,0,-0.87), area 3.6mm2, adj f2,f3,f171,f173
  f173: cylinder r=0.5mm len=15mm, axis (0,1,0), area 9.8mm2, adj f2,f3,f172,f174
  f174: plane 15x1.14mm, normal (0.97,0,0.25), area 17.7mm2, adj f2,f3,f173,f175
  f175: cylinder r=0.5mm len=15mm, axis (0,1,0), area 9.8mm2, adj f2,f3,f174,f176
  f176: plane 15x0.24mm, normal (0.01,0,1), area 3.6mm2, adj f2,f3,f175,f177
  f177: cylinder r=0.3mm len=15mm, axis (0,1,0), area 12.3mm2, adj f2,f3,f176,f178
  f178: plane 15x0.22mm, normal (0.4,0,-0.92), area 3.6mm2, adj f2,f3,f177,f179
  f179: cylinder r=0.5mm len=15mm, axis (0,1,0), area 9.8mm2, adj f2,f3,f178,f180
  f180: plane 15x1.17mm, normal (0.99,0,0.15), area 17.7mm2, adj f2,f3,f179,f181
  f181: cylinder r=0.5mm len=15mm, axis (0,1,0), area 9.8mm2, adj f2,f3,f180,f182
  f182: plane 15x0.24mm, normal (0.11,0,0.99), area 3.6mm2, adj f2,f3,f181,f183
  f183: cylinder r=0.3mm len=15mm, axis (0,1,0), area 12.3mm2, adj f2,f3,f182,f184
  f184: plane 15x0.23mm, normal (0.3,0,-0.96), area 3.6mm2, adj f2,f3,f183,f185
  f185: cylinder r=0.5mm len=15mm, axis (0,1,0), area 9.8mm2, adj f2,f3,f184,f186
  f186: plane 15x1.18mm, normal (1,0,0.04), area 17.7mm2, adj f2,f3,f185,f187
  f187: cylinder r=0.5mm len=15mm, axis (0,1,0), area 9.8mm2, adj f2,f3,f186,f188
  f188: plane 15x0.6mm, normal (0.21,0,0.98), area 9.2mm2, adj f2,f3,f9,f187
PLACE A t=(-18.69,13.86,-13.26)mm
PLACE B t=(-43.66,102.8,-13.19)mm fixed
PLACE C t=(-18.69,13.86,11.74)mm
MATE fastened C.f8 <-> A.f7  axis (0,0,1) through (-93.69,6.36,-13.26)mm
MATE slider B.f1 <-> A.f5  axis (0,1,0) through (-43.66,2.8,-13.19)mm
